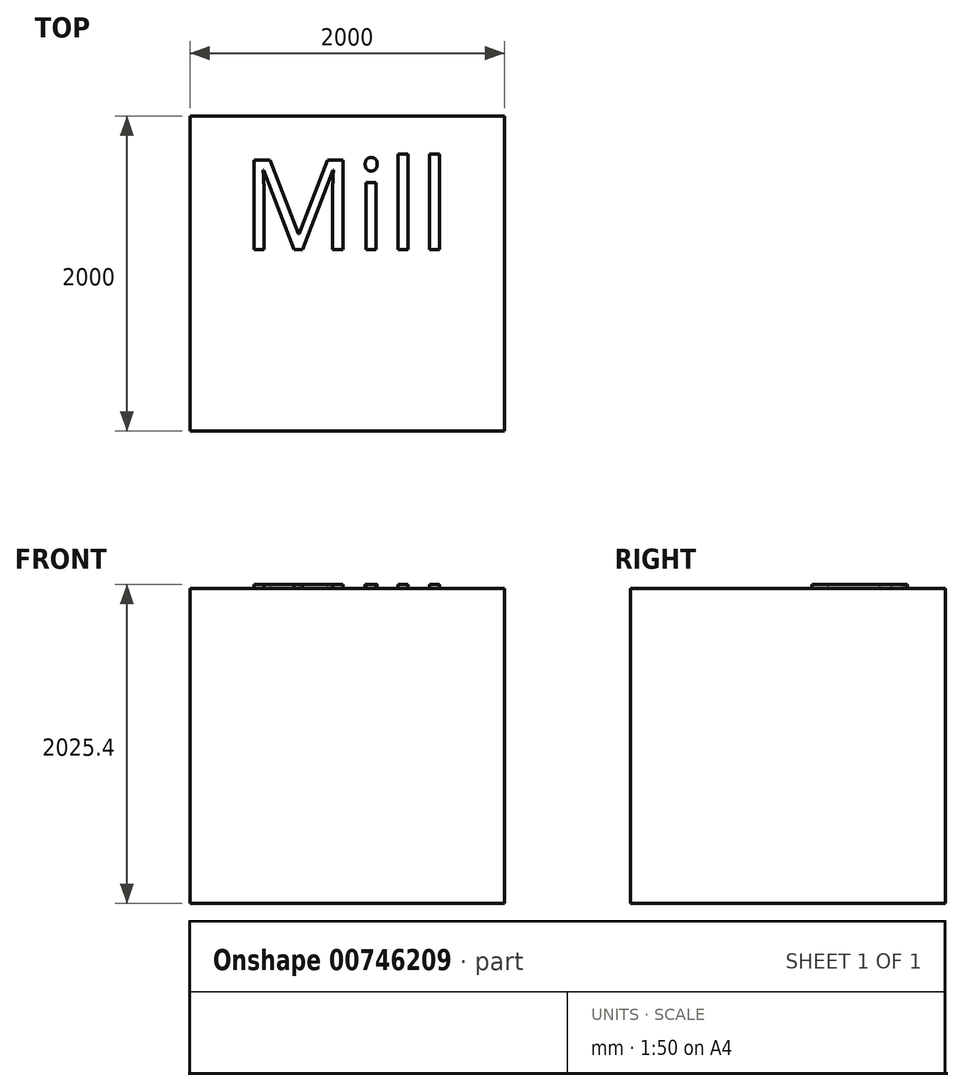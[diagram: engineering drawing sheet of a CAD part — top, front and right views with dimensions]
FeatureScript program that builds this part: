
annotation { "Feature Type Name" : "Feature", "Feature Type Description" : "" }
export const myFeature = defineFeature(function(context is Context, id is Id, definition is map)
    precondition{}
    {
        {
            var Q0;
            Q0=qCreatedBy(makeId("Top.planeOp"),FACE);
            var sketch = newSketch(context, id + "F0", { "sketchPlane" : qUnion([Q0])});
            skLineSegment(sketch, "E0.bottom", {"start": v(1014.99, -1000) * mm, "end": v(-985.01, -1000) * mm});
            skLineSegment(sketch, "E0.top", {"start": v(1014.99, 1000) * mm, "end": v(-985.01, 1000) * mm});
            skLineSegment(sketch, "E0.left", {"start": v(1014.99, -1000) * mm, "end": v(1014.99, 1000) * mm});
            skLineSegment(sketch, "E0.right", {"start": v(-985.01, -1000) * mm, "end": v(-985.01, 1000) * mm});
            skPoint(sketch, "E0.middle", {"position": v(14.99, 0) * mm});
            skSolve(sketch);
        }
        {
            var Q0;
            Q0 = qSketchRegion(id + "F0", true);
            extrude(context, id + "F1", {"entities" : qUnion([Q0]), "depth" : 2000 * mm, "offsetDistance" : 25.4 * mm});
        }
        {
            var Q0;
            Q0=makeQuery(id+"F1.opExtrude","CAP_FACE",FACE,{"disambiguationData":[OSD([sQuery(id+"F0.wireOp",EDGE,"E0.bottom"),sQuery(id+"F0.wireOp",EDGE,"E0.top"),sQuery(id+"F0.wireOp",EDGE,"E0.left"),sQuery(id+"F0.wireOp",EDGE,"E0.right")])],"isStart":false});
            var sketch = newSketch(context, id + "F2", { "sketchPlane" : qUnion([Q0])});
            skText(sketch, "E1", { "text": "Mill\n", "fontName": "OpenSans-Regular.ttf"});
            const initialGuessF2  = {"E1": [-0.65379, 0.15262, 1, 0, 0.57384]};
            skSetInitialGuess(sketch, initialGuessF2);
            skSolve(sketch);
        }
        {
            var Q0;
            Q0 = qSketchRegion(id + "F2", true);
            extrude(context, id + "F3", {"entities" : qUnion([Q0]), "operationType" : NewBodyOperationType.ADD, "depth" : 25.4 * mm, "offsetDistance" : 25.4 * mm});
        }
    });
